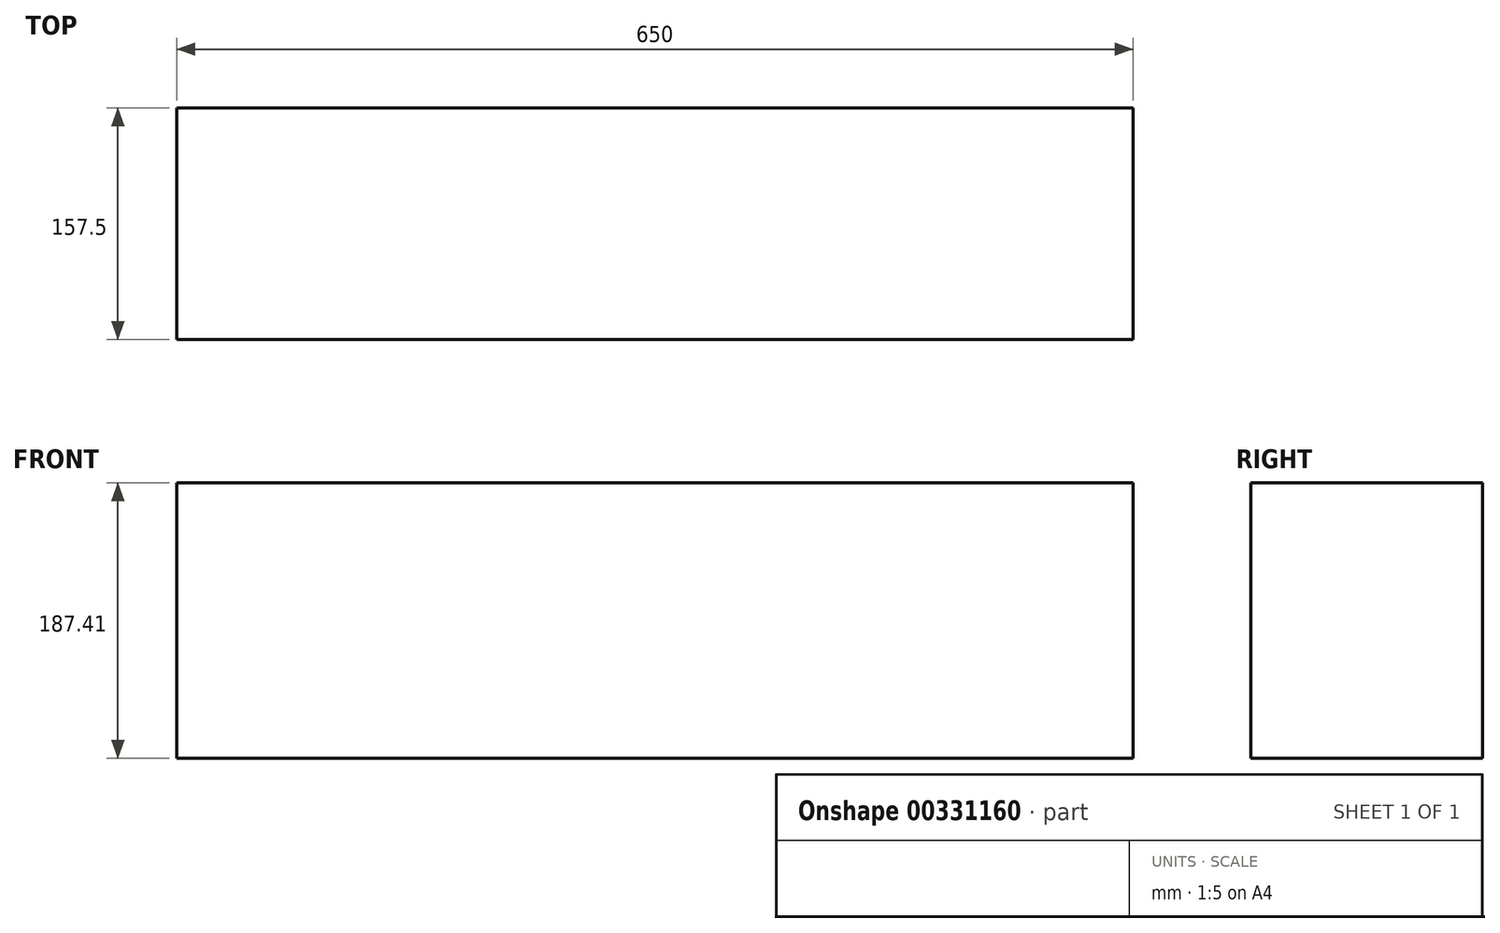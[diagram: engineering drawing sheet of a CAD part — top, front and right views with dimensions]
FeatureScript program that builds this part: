
annotation { "Feature Type Name" : "Feature", "Feature Type Description" : "" }
export const myFeature = defineFeature(function(context is Context, id is Id, definition is map)
    precondition{}
    {
        {
            var Q0;
            Q0=qCreatedBy(makeId("Right.planeOp"),FACE);
            var sketch = newSketch(context, id + "F0", { "sketchPlane" : qUnion([Q0])});
            skLineSegment(sketch, "E0.bottom", {"start": v(-74.84, 74.95) * mm, "end": v(82.66, 74.95) * mm});
            skLineSegment(sketch, "E0.top", {"start": v(-74.84, -112.46) * mm, "end": v(82.66, -112.46) * mm});
            skLineSegment(sketch, "E0.left", {"start": v(-74.84, 74.95) * mm, "end": v(-74.84, -112.46) * mm});
            skLineSegment(sketch, "E0.right", {"start": v(82.66, 74.95) * mm, "end": v(82.66, -112.46) * mm});
            skSolve(sketch);
        }
        {
            var Q0;
            Q0=makeQuery(id+"F0.imprint","IMPRINT",FACE,{"disambiguationData":[TD([[makeQuery(id+"F0.imprint","IMPRINT",EDGE,{"derivedFrom":sQuery(id+"F0.wireOp",EDGE,"E0.bottom")}),-1.0]])]});
            var Q1;
            Q1=sQuery(id+"F0.wireOp",EDGE,"E0.right");
            extrude(context, id + "F1", {"entities" : qUnion([Q0]), "surfaceEntities" : qUnion([Q1]), "depth" : 650 * mm});
        }
    });
